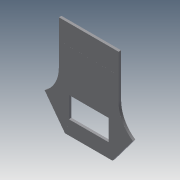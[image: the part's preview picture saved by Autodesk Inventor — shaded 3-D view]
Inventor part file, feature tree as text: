
AUTODESK INVENTOR PART (.ipt)
format: ipt  version: 2013 (Build 170138000, 138)  size: 1,100,288 bytes
history: native  units: mm
features: sketch x98, extrude x87, fillet x2
ambient origin geometry x8: Origin, YZ Plane, XZ Plane, XY Plane, X Axis, Y Axis, Z Axis, Center Point
bodies: Solid1 (feature_tree)
feature tree (187):
  extrude  "Extrusion1"  Depth=10.0mm
  extrude  "Extrusion2"  Depth=10.0mm
  sketch  "Sketch3"  dims[d8=2.0mm d9=0.0mm d11=3.0mm]
  extrude  "Extrusion3"  Depth=3.0mm
  extrude  "Extrusion4"  Depth=3.0mm
  extrude  "Extrusion5"  Depth=10.0mm TaperAngle=0.0deg
  extrude  "Extrusion6"  Depth=3.0mm
  sketch  "Sketch8"  dims[d24=10.0mm d25=0.0mm d26=2.0mm d27=0.0mm]
  extrude  "Extrusion7"  Depth=3.0mm
  extrude  "Extrusion8"  Depth=2.0mm TaperAngle=0.0deg
  extrude  "Extrusion9"  Depth=3.0mm
  extrude  "Extrusion10"  Depth=2.0mm TaperAngle=0.0deg
  extrude  "Extrusion11"  Depth=4.0mm
  extrude  "Extrusion12"  Depth=4.0mm
  extrude  "Extrusion13"  Depth=1.8mm
  sketch  "Sketch16"  dims[d61=4.0mm d62=4.0mm]
  extrude  "Extrusion14"  Depth=4.0mm
  extrude  "Extrusion15"  Depth=12.0mm
  extrude  "Extrusion16"  Depth=4.0mm
  extrude  "Extrusion17"  Depth=16.0mm
  sketch  "Sketch21"  dims[d75=30.0mm d77=2.0mm d78=0.0mm]
  extrude  "Extrusion18"  Depth=10.4mm
  extrude  "Extrusion19"  Depth=4.0mm
  extrude  "Extrusion20"  Depth=20.0mm
  extrude  "Extrusion21"  Depth=2.0mm TaperAngle=0.0deg
  extrude  "Extrusion22"  Depth=2.3mm
  extrude  "Extrusion23"  Depth=24.0mm
  extrude  "Extrusion24"  Depth=2.0mm TaperAngle=0.0deg
  extrude  "Extrusion25"  Depth=3.0mm
  extrude  "Extrusion26"  Depth=2.0mm TaperAngle=0.0deg
  extrude  "Extrusion27"  Depth=2.0mm TaperAngle=0.0deg
  extrude  "Extrusion28"  Depth=4.0mm
  extrude  "Extrusion29"  Depth=3.0mm
  extrude  "Extrusion30"  Depth=3.0mm
  extrude  "Extrusion31"  Depth=3.0mm
  extrude  "Extrusion32"  Depth=4.0mm
  extrude  "Extrusion33"  Depth=3.0mm
  extrude  "Extrusion34"  Depth=2.0mm TaperAngle=0.0deg
  extrude  "Extrusion35"  Depth=2.3mm
  extrude  "Extrusion36"  Depth=4.0mm
  extrude  "Extrusion37"  Depth=2.3mm
  sketch  "Sketch42"  dims[d147=24.0mm d148=24.0mm]
  sketch  "Sketch43"  dims[d149=2.0mm d150=0.0mm d151=2.0mm d152=0.0mm]
  extrude  "Extrusion38"  Depth=2.0mm TaperAngle=0.0deg
  extrude  "Extrusion39"  Depth=2.0mm TaperAngle=0.0deg
  extrude  "Extrusion40"  Depth=20.0mm
  extrude  "Extrusion41"  Depth=20.0mm
  extrude  "Extrusion42"  Depth=24.0mm
  extrude  "Extrusion43"  Depth=2.0mm TaperAngle=0.0deg
  extrude  "Extrusion44"  Depth=3.0mm
  extrude  "Extrusion45"  Depth=20.0mm
  extrude  "Extrusion46"  Depth=2.0mm TaperAngle=0.0deg
  extrude  "Extrusion47"  Depth=3.0mm
  extrude  "Extrusion48"  Depth=3.0mm
  fillet  "Fillet1"  Radius=3.0mm
  extrude  "Extrusion49"  Depth=2.5mm
  fillet  "Fillet2"  Radius=2.0mm
  extrude  "Extrusion50"  Depth=12.5mm
  extrude  "Extrusion51"  Depth=2.5mm
  extrude  "Extrusion52"  Depth=20.0mm
  extrude  "Extrusion53"  Depth=25.0mm
  extrude  "Extrusion54"  Depth=2.0mm TaperAngle=0.0deg
  extrude  "Extrusion55"  Depth=1.5mm
  extrude  "Extrusion56"  Depth=20.0mm
  extrude  "Extrusion57"  Depth=20.0mm
  extrude  "Extrusion58"  Depth=24.0mm
  extrude  "Extrusion59"  Depth=3.4mm
  extrude  "Extrusion60"  Depth=3.0mm
  extrude  "Extrusion61"  Depth=3.0mm
  extrude  "Extrusion62"  Depth=2.0mm TaperAngle=0.0deg
  sketch  "Sketch67"  dims[d218=3.0mm d219=3.0mm]
  extrude  "Extrusion63"  Depth=17.0mm
  extrude  "Extrusion64"  Depth=2.0mm TaperAngle=0.0deg
  extrude  "Extrusion65"  Depth=14.4mm
  sketch  "Sketch71"  dims[d228=1.5mm d229=3.0mm]
  sketch  "Sketch72"  dims[d230=2.0mm d231=0.0mm d233=2.0mm d234=0.0mm]
  extrude  "Extrusion66"  Depth=1.5mm
  sketch  "Sketch73"  dims[d236=14.5mm d237=13.95mm]
  sketch  "Sketch74"  dims[d238=13.95mm d239=3.0mm]
  extrude  "Extrusion67"  Depth=3.0mm
  extrude  "Extrusion68"  Depth=2.0mm TaperAngle=0.0deg
  extrude  "Extrusion69"  Depth=1.5mm
  extrude  "Extrusion70"  Depth=14.4mm
  extrude  "Extrusion71"  Depth=3.0mm
  sketch  "Sketch80"  dims[d256=19.0mm d259=19.0mm]
  sketch  "Sketch81"  dims[d260=2.0mm d261=0.0mm d262=10.0mm]
  extrude  "Extrusion72"  Depth=2.0mm TaperAngle=0.0deg
  extrude  "Extrusion73"  Depth=13.95mm
  sketch  "Sketch84"  dims[d269=2.0mm d270=0.0mm d271=2.0mm d272=0.0mm]
  extrude  "Extrusion74"  Depth=3.0mm
  extrude  "Extrusion75"  Depth=2.0mm TaperAngle=0.0deg
  extrude  "Extrusion76"  Depth=14.4mm
  extrude  "Extrusion77"  Depth=2.0mm
  extrude  "Extrusion78"  Depth=4.0mm
  extrude  "Extrusion79"  Depth=2.0mm TaperAngle=0.0deg
  extrude  "Extrusion80"  Depth=19.0mm
  extrude  "Extrusion81"  Depth=10.0mm
  extrude  "Extrusion82"  Depth=4.0mm
  extrude  "Extrusion83"  Depth=2.0mm TaperAngle=0.0deg
  extrude  "Extrusion84"  Depth=2.0mm TaperAngle=0.0deg
  extrude  "Extrusion85"  Depth=2.0mm TaperAngle=0.0deg
  extrude  "Extrusion86"  Depth=10.0mm TaperAngle=0.0deg
  extrude  "Extrusion87"  Depth=0.5mm TaperAngle=0.0deg
  sketch  "Sketch1"  dims[d2=10.0mm d3=10.0mm]
  sketch  "Sketch2"  dims[d4=10.0mm d7=10.0mm]
  sketch  "Sketch4"  dims[d12=3.0mm d14=3.0mm]
  sketch  "Sketch5"  dims[d15=3.0mm d16=10.0mm d17=0.0mm]
  sketch  "Sketch6"  dims[d20=6.0mm d21=3.0mm]
  sketch  "Sketch7"  dims[d22=6.0mm d23=3.0mm]
  sketch  "Sketch9"  dims[d34=3.0mm d36=3.0mm]
  sketch  "Sketch10"  dims[d37=2.0mm d38=0.0mm d39=2.0mm d40=0.0mm]
  sketch  "Sketch11"  dims[d48=2.0mm d49=4.0mm]
  sketch  "Sketch12"  dims[d51=12.0mm d52=4.0mm]
  sketch  "Sketch13"  dims[d53=2.0mm d54=0.0mm d55=1.8mm]
  sketch  "Sketch14"  dims[d56=2.0mm d57=4.0mm]
  sketch  "Sketch15"  dims[d58=2.0mm d59=0.0mm d60=12.0mm]
  sketch  "Sketch17"  dims[d63=2.0mm d64=0.0mm d65=16.0mm]
  sketch  "Sketch18"  dims[d66=12.0mm d67=10.4mm]
  sketch  "Sketch19"  dims[d68=2.0mm d69=0.0mm d70=4.0mm]
  sketch  "Sketch20"  dims[d71=2.0mm d72=0.0mm d74=20.0mm]
  sketch  "Sketch22"  dims[d83=2.3mm d84=2.3mm]
  sketch  "Sketch23"  dims[d85=2.0mm d86=0.0mm d90=24.0mm]
  sketch  "Sketch24"  dims[d92=24.0mm d93=2.0mm d94=0.0mm]
  sketch  "Sketch25"  dims[d97=3.0mm d98=3.0mm]
  sketch  "Sketch26"  dims[d100=3.0mm d101=2.0mm d102=0.0mm]
  sketch  "Sketch27"  dims[d103=2.0mm d104=0.0mm d105=2.0mm d106=0.0mm]
  sketch  "Sketch28"  dims[d111=4.0mm d112=4.0mm]
  sketch  "Sketch29"  dims[d113=3.0mm d114=3.0mm]
  sketch  "Sketch30"  dims[d116=3.0mm d117=3.0mm]
  sketch  "Sketch31"  dims[d118=3.0mm d119=3.0mm]
  sketch  "Sketch32"  dims[d120=3.0mm d121=4.0mm]
  sketch  "Sketch33"  dims[d122=3.0mm d123=3.0mm]
  sketch  "Sketch34"  dims[d124=3.0mm d125=2.0mm d126=0.0mm]
  sketch  "Sketch35"  dims[d127=2.3mm d128=2.3mm]
  sketch  "Sketch36"  dims[d131=4.0mm d132=4.0mm]
  sketch  "Sketch37"  dims[d133=2.0mm d134=0.0mm d135=2.3mm]
  sketch  "Sketch38"  dims[d136=2.3mm d137=2.0mm d138=0.0mm]
  sketch  "Sketch39"  dims[d139=3.0mm d140=2.0mm d141=0.0mm]
  sketch  "Sketch40"  dims[d142=2.0mm d143=0.0mm d144=20.0mm]
  sketch  "Sketch41"  dims[d145=14.0mm d146=20.0mm]
  sketch  "Sketch44"  dims[d157=3.0mm d158=3.0mm]
  sketch  "Sketch45"  dims[d159=2.0mm d160=0.0mm d161=20.0mm]
  sketch  "Sketch46"  dims[d162=20.0mm d163=2.0mm d164=0.0mm]
  sketch  "Sketch47"  dims[d165=2.0mm d166=0.0mm d167=3.0mm]
  sketch  "Sketch48"  dims[d168=3.0mm d169=3.0mm d170=3.0mm]
  sketch  "Sketch49"  dims[d171=2.5mm d172=2.5mm d173=2.0mm d174=0.0mm]
  sketch  "Sketch50"  dims[d175=2.0mm d176=0.0mm d178=12.5mm]
  sketch  "Sketch51"  dims[d179=12.5mm d180=2.5mm]
  sketch  "Sketch52"  dims[d181=2.5mm d183=20.0mm]
  sketch  "Sketch53"  dims[d185=20.0mm d186=25.0mm]
  sketch  "Sketch54"  dims[d187=25.0mm d188=2.0mm d189=0.0mm]
  sketch  "Sketch55"  dims[d190=1.5mm d191=1.5mm]
  sketch  "Sketch56"  dims[d192=1.5mm d193=20.0mm]
  sketch  "Sketch57"  dims[d194=1.5mm d195=20.0mm]
  sketch  "Sketch58"  dims[d196=24.0mm d197=24.0mm]
  sketch  "Sketch59"  dims[d198=2.0mm d199=0.0mm d200=3.4mm]
  sketch  "Sketch60"  dims[d201=3.4mm d202=3.0mm]
  sketch  "Sketch61"  dims[d203=3.0mm d204=3.0mm]
  sketch  "Sketch62"  dims[d205=3.0mm d206=2.0mm d207=0.0mm]
  sketch  "Sketch63"  dims[d208=2.0mm d209=0.0mm d210=17.0mm]
  sketch  "Sketch64"  dims[d211=14.4mm d212=2.0mm d213=0.0mm]
  sketch  "Sketch65"  dims[d214=19.5mm d215=14.4mm]
  sketch  "Sketch66"  dims[d216=1.5mm d217=1.5mm]
  sketch  "Sketch68"  dims[d220=2.0mm d221=0.0mm d222=2.0mm d223=0.0mm]
  sketch  "Sketch69"  dims[d224=19.5mm d225=1.5mm]
  sketch  "Sketch70"  dims[d226=3.0mm d227=14.4mm]
  sketch  "Sketch75"  dims[d241=3.0mm d242=2.0mm d243=0.0mm]
  sketch  "Sketch76"  dims[d244=2.0mm d245=0.0mm d248=14.4mm]
  sketch  "Sketch77"  dims[d249=21.6mm d250=2.0mm]
  sketch  "Sketch78"  dims[d251=2.0mm d252=4.0mm]
  sketch  "Sketch79"  dims[d253=4.0mm d254=2.0mm d255=0.0mm]
  sketch  "Sketch82"  dims[d263=4.0mm d264=4.0mm]
  sketch  "Sketch83"  dims[d265=2.0mm d266=0.0mm d267=2.0mm d268=0.0mm]
  sketch  "Sketch85"  dims[d273=3.6mm d274=2.0mm d275=0.0mm]
  sketch  "Sketch86"  dims[d276=1.5mm d277=10.0mm d278=0.0mm]
  sketch  "Sketch87"  dims[d279=2.0mm d280=0.5mm d281=0.0mm]
  sketch  "Sketch88"  dims[d282=0.5mm]
  sketch  "Sketch89"  dims[d283=1.5mm d284=0.0mm]
  sketch  "Sketch90"  dims[d285=1.5mm d286=0.0mm]
  sketch  "Sketch91"  dims[d287=10.4mm]
  sketch  "Sketch92"  dims[d288=14.398895mm]
  sketch  "Sketch93"  dims[d289=16.0mm]
  sketch  "Sketch94"  dims[d290=1.5mm d291=0.0mm]
  sketch  "Sketch95"  dims[d292=1.5mm d293=0.0mm]
  sketch  "Sketch96"  dims[d294=10.0mm d295=0.0mm]
  sketch  "Sketch97"  dims[d296=10.0mm d297=0.0mm]
  sketch  "Sketch98"  dims[d298=10.0mm d299=0.0mm d300=20.0mm d301=0.0mm d306=1.5mm d307=0.0mm d308=4.0mm d309=7.0mm d310=16.0mm d311=3.0mm d312=7.0mm d313=16.0mm d314=1.5mm d315=0.0mm d316=5.0mm d317=1.5mm d318=0.0mm d319=1.5mm d320=10.0mm d321=0.0mm d322=7.0mm d323=7.0mm d324=4.0mm d325=7.0mm d326=4.0mm d327=7.0mm d328=4.0mm d329=1.5mm d330=0.0mm d331=4.0mm d332=4.129mm d333=7.0mm d335=3.072mm d336=7.0mm d337=15.0mm d338=1.5mm d339=0.0mm d341=1.5mm d342=0.0mm d343=0.5mm d344=7.0mm d345=18.0mm d346=7.0mm d347=1.5mm d348=0.0mm d349=7.0mm d351=7.0mm d353=1.5mm d354=0.0mm d359=8.3mm d360=11.6mm d361=23.6mm d362=12.4mm d363=1.5mm d364=0.0mm d365=27.9mm d366=0.4mm d367=1.5mm d368=0.0mm d370=0.3mm d371=0.3mm d372=1.5mm d373=0.0mm d374=5.0mm d375=5.0mm d376=1.5mm d377=0.0mm d378=6.3mm d379=12.6mm d380=3.0mm d381=3.0mm d382=1.5mm d383=0.0mm d391=1.5mm d392=0.0mm d395=7.0mm d396=19.0mm d399=7.0mm d400=1.5mm d401=0.0mm d403=1.5mm d404=0.0mm d406=1.5mm d407=3.0mm d409=1.5mm d410=3.0mm d411=1.5mm d412=0.0mm d413=14.5mm d414=3.0mm d415=1.5mm d416=0.0mm d417=3.0mm d418=1.5mm d419=3.0mm d420=2.0mm d421=3.0mm d422=3.0mm d423=1.5mm d424=0.0mm d425=1.5mm d426=1.5mm d427=0.0mm d428=1.5mm d429=1.5mm d430=0.0mm d431=1.5mm d432=0.0mm d433=3.0mm d434=3.0mm d435=3.0mm d436=3.0mm d437=1.5mm d438=0.0mm d439=1.5mm d440=0.0mm d441=3.0mm d442=3.0mm d443=1.5mm d444=0.0mm d445=10.0mm d446=0.0mm d447=12.0mm d449=0.01mm d451=0.01mm d452=1.5mm d453=0.0mm d454=6.5mm d456=6.3mm d457=6.3mm d460=0.1mm d461=0.1mm d462=0.1mm d463=1.5mm d464=0.0mm d465=0.1mm d466=0.1mm d467=0.1mm d468=0.1mm d469=0.1mm d470=0.1mm d471=0.1mm d472=0.1mm d473=1.5mm d474=0.0mm]
